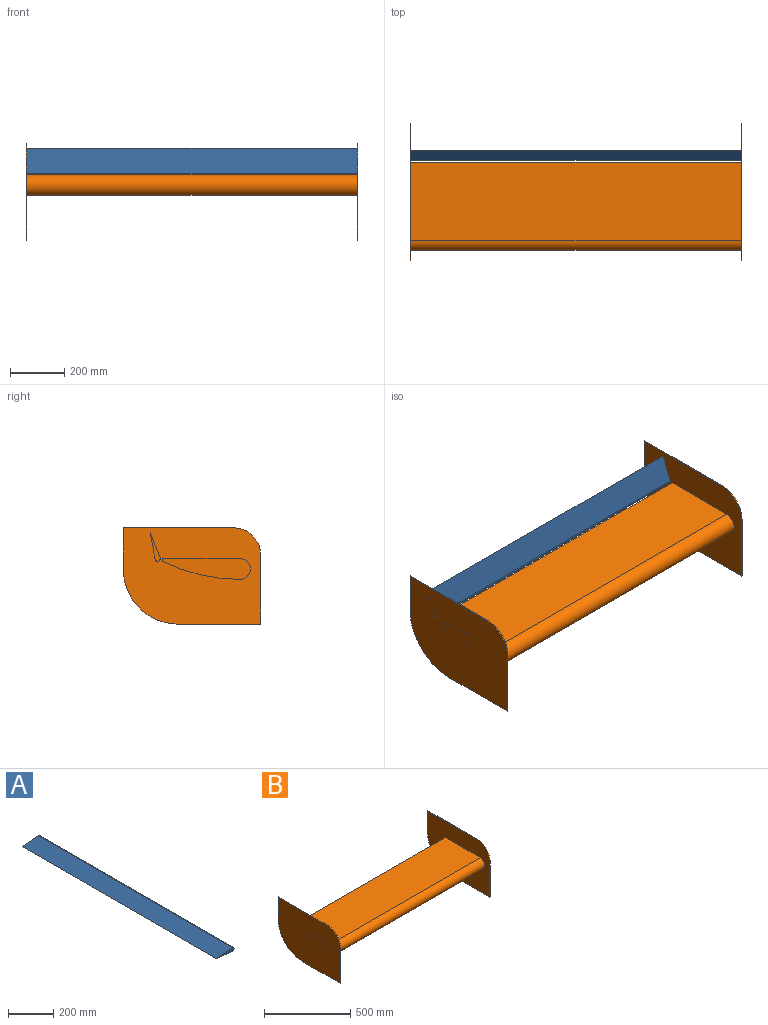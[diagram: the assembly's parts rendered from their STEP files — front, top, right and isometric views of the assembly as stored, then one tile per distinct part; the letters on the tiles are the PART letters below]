
ASSEMBLY  parts=2 mates=1
PART A: 5 faces, bbox 111.1x1219.2x19.1 mm
  f0: plane 1219.2x100.71mm, normal (-0.09,0,1), area 123325.2mm2, adj f1,f2,f3,f4
  f1: plane 1219.2x100.71mm, normal (-0.09,0,-1), area 123325.2mm2, adj f0,f2,f3,f4
  f2: cylinder r=9.53mm len=1219.2mm, axis (0,1,0), area 38663.6mm2, adj f0,f1,f3,f4
  f3: plane 111.13x19.05mm, normal (0,-1,0), area 1114.5mm2, adj f0,f1,f2
  f4: plane 111.13x19.05mm, normal (0,1,0), area 1114.5mm2, adj f0,f1,f2
PART B: 20 faces, bbox 1225.6x508x355.6 mm
  f0: cylinder r=38.1mm len=1219.2mm, axis (-1,0,0), area 145931.8mm2, adj f1,f2,f4,f12
  f1: cylinder r=647.7mm len=1219.2mm, axis (-1,0,0), area 363734mm2, adj f0,f3,f4,f12
  f2: plane 1219.2x285.64mm, normal (0,0,1), area 348249.7mm2, adj f0,f3,f4,f12
  f3: cylinder r=19.05mm len=1219.2mm, axis (1,0,0), area 11060.7mm2, adj f1,f2,f4,f12
  f4: plane 508x355.6mm, normal (1,0,0), area 151700.2mm2, adj f0,f1,f2,f3,f5,f6,f7,f8
  f5: plane 304.8x3.18mm, normal (0,0,-1), area 967.7mm2, adj f4,f6,f10,f11
  f6: plane 254x3.18mm, normal (0,-1,0), area 806.4mm2, adj f4,f5,f7,f11
  f7: cylinder r=101.6mm len=101.6mm, axis (1,0,0), area 506.7mm2, adj f4,f6,f8,f11
  f8: plane 406.4x3.18mm, normal (0,0,1), area 1290.3mm2, adj f4,f7,f9,f11
  f9: plane 152.4x3.18mm, normal (0,1,0), area 483.9mm2, adj f4,f8,f10,f11
  f10: cylinder r=203.2mm len=203.2mm, axis (1,0,0), area 1013.4mm2, adj f4,f5,f9,f11
  f11: plane 508x355.6mm, normal (-1,0,0), area 169568.6mm2, adj f5,f6,f7,f8,f9,f10
  f12: plane 508x355.6mm, normal (-1,0,0), area 151700.2mm2, adj f0,f1,f2,f3,f13,f14,f15,f16
  f13: plane 304.8x3.18mm, normal (0,0,-1), area 967.7mm2, adj f12,f14,f18,f19
  f14: plane 254x3.18mm, normal (0,-1,0), area 806.4mm2, adj f12,f13,f15,f19
  f15: cylinder r=101.6mm len=101.6mm, axis (-1,0,0), area 506.7mm2, adj f12,f14,f16,f19
  f16: plane 406.4x3.18mm, normal (0,0,1), area 1290.3mm2, adj f12,f15,f17,f19
  f17: plane 152.4x3.18mm, normal (0,1,0), area 483.9mm2, adj f12,f16,f18,f19
  f18: cylinder r=203.2mm len=203.2mm, axis (-1,0,0), area 1013.4mm2, adj f12,f13,f17,f19
  f19: plane 508x355.6mm, normal (1,0,0), area 169568.6mm2, adj f13,f14,f15,f16,f17,f18
PLACE A rot(axis=(0.52,0.52,-0.68),111.4deg) t=(-2.36,127.28,66.45)mm
PLACE B t=(-2.36,-101.2,28.04)mm fixed
MATE revolute A.f2 <-> B.f3  axis (1,0,0) through (-2.36,127.28,66.45)mm
